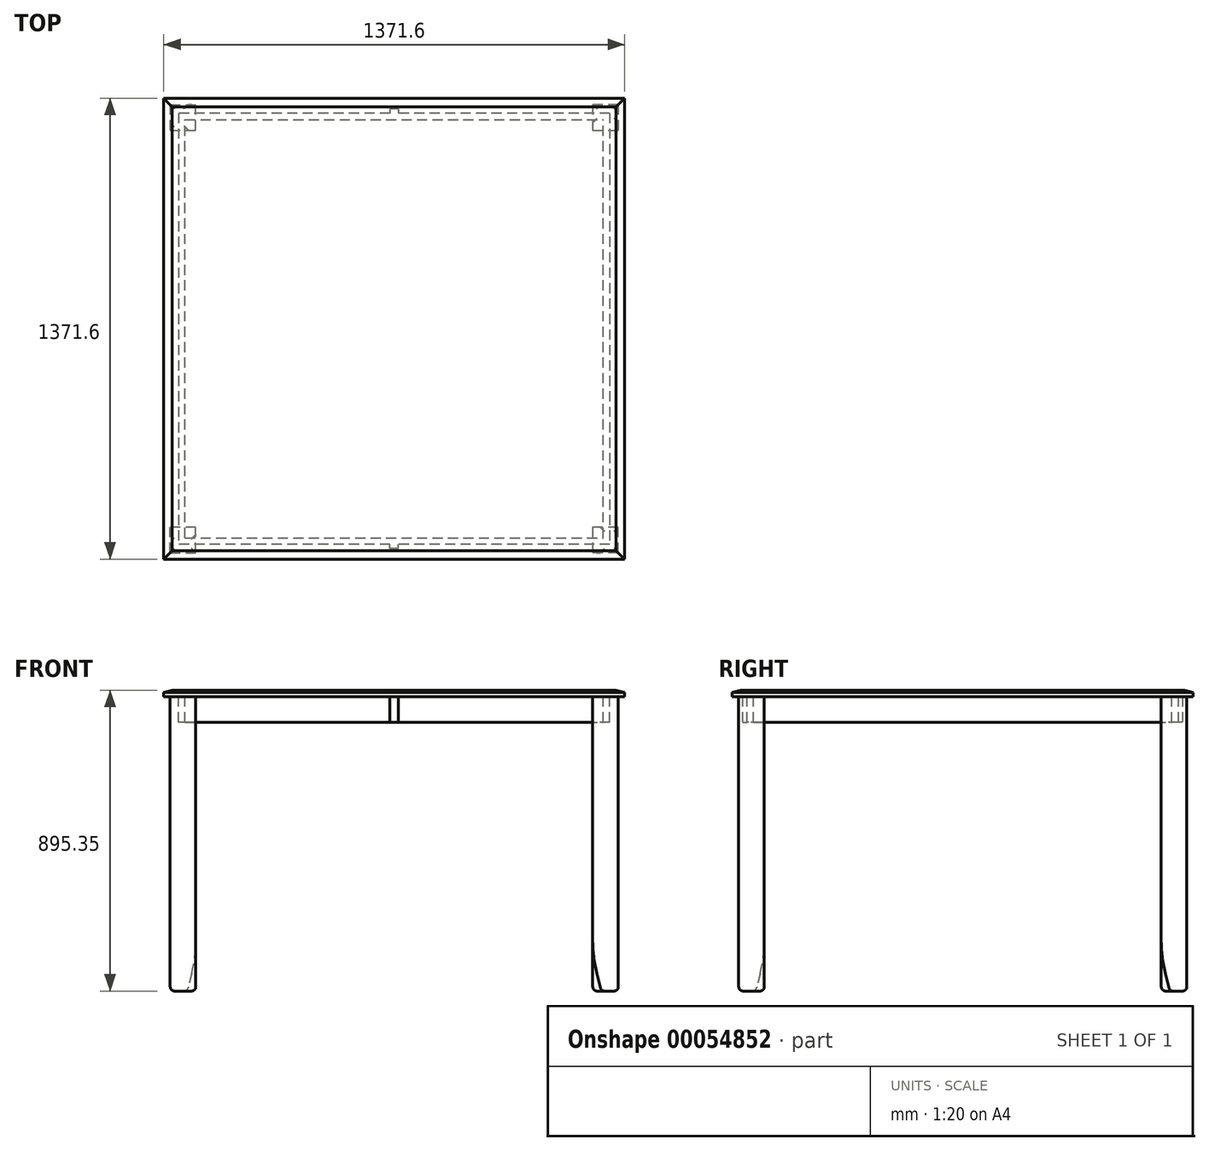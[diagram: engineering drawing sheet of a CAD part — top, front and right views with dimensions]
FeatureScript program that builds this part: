
annotation { "Feature Type Name" : "Feature", "Feature Type Description" : "" }
export const myFeature = defineFeature(function(context is Context, id is Id, definition is map)
    precondition{}
    {
        {
            var Q0;
            Q0=qCreatedBy(makeId("Top.planeOp"),FACE);
            var sketch = newSketch(context, id + "F0", { "sketchPlane" : qUnion([Q0])});
            skLineSegment(sketch, "E0.rect.bottom", {"start": v(685.8, 685.8) * mm, "end": v(-685.8, 685.8) * mm});
            skLineSegment(sketch, "E0.rect.top", {"start": v(685.8, -685.8) * mm, "end": v(-685.8, -685.8) * mm});
            skLineSegment(sketch, "E0.rect.left", {"start": v(685.8, 685.8) * mm, "end": v(685.8, -685.8) * mm});
            skLineSegment(sketch, "E0.rect.right", {"start": v(-685.8, 685.8) * mm, "end": v(-685.8, -685.8) * mm});
            skPoint(sketch, "E0.rect.middle", {"position": v(0, 0) * mm});
            skSolve(sketch);
        }
        {
            var Q0;
            Q0=qSketchRegion(id+"F0",true);
            extrude(context, id + "F1", {"entities" : qUnion([Q0]), "oppositeDirection" : true, "depth" : 19.05 * mm});
        }
        {
            var Q0;
            Q0=makeQuery(id+"F1.opExtrude","CAP_FACE",FACE,{"disambiguationData":[OSD([sQuery(id+"F0.wireOp",EDGE,"E0.rect.bottom"),sQuery(id+"F0.wireOp",EDGE,"E0.rect.top"),sQuery(id+"F0.wireOp",EDGE,"E0.rect.left"),sQuery(id+"F0.wireOp",EDGE,"E0.rect.right")])],"isStart":false});
            var sketch = newSketch(context, id + "F2", { "sketchPlane" : qUnion([Q0])});
            skLineSegment(sketch, "E1.rect.bottom", {"start": v(641.35, -641.35) * mm, "end": v(-641.35, -641.35) * mm});
            skLineSegment(sketch, "E1.rect.top", {"start": v(641.35, 641.35) * mm, "end": v(-641.35, 641.35) * mm});
            skLineSegment(sketch, "E1.rect.left", {"start": v(641.35, -641.35) * mm, "end": v(641.35, 641.35) * mm});
            skLineSegment(sketch, "E1.rect.right", {"start": v(-641.35, -641.35) * mm, "end": v(-641.35, 641.35) * mm});
            skPoint(sketch, "E1.rect.middle", {"position": v(0, 0) * mm});
            skLineSegment(sketch, "E2.rect.bottom", {"start": v(-622.3, 622.3) * mm, "end": v(622.3, 622.3) * mm});
            skLineSegment(sketch, "E2.rect.top", {"start": v(-622.3, -622.3) * mm, "end": v(622.3, -622.3) * mm});
            skLineSegment(sketch, "E2.rect.left", {"start": v(-622.3, 622.3) * mm, "end": v(-622.3, -622.3) * mm});
            skLineSegment(sketch, "E2.rect.right", {"start": v(622.3, 622.3) * mm, "end": v(622.3, -622.3) * mm});
            skSolve(sketch);
        }
        {
            var Q0;
            Q0=qSketchRegion(id+"F2",true);
            extrude(context, id + "F3", {"entities" : qUnion([Q0]), "operationType" : NewBodyOperationType.ADD, "depth" : 76.2 * mm});
        }
        {
            var Q0;
            {var subQ0=sQuery(id+"F0.wireOp",EDGE,"E0.rect.right");var subQ1=sQuery(id+"F0.wireOp",EDGE,"E0.rect.left");var subQ2=sQuery(id+"F0.wireOp",EDGE,"E0.rect.top");var subQ3=sQuery(id+"F0.wireOp",EDGE,"E0.rect.bottom");Q0=makeQuery(id+"F3.boolean.opBoolean","SPLIT",FACE,{"disambiguationData":[TD([makeQuery(id+"F1.opExtrude","SWEPT_FACE",FACE,{"disambiguationData":[OSD([subQ3])]})])],"derivedFrom":makeQuery(id+"F1.opExtrude","CAP_FACE",FACE,{"disambiguationData":[OSD([subQ3,subQ2,subQ1,subQ0])],"isStart":false})});}
            var sketch = newSketch(context, id + "F4", { "sketchPlane" : qUnion([Q0])});
            skLineSegment(sketch, "E3.bottom", {"start": v(-666.75, 666.75) * mm, "end": v(-590.55, 666.75) * mm});
            skLineSegment(sketch, "E3.top", {"start": v(-666.75, 590.55) * mm, "end": v(-590.55, 590.55) * mm});
            skLineSegment(sketch, "E3.left", {"start": v(-666.75, 666.75) * mm, "end": v(-666.75, 590.55) * mm});
            skLineSegment(sketch, "E3.right", {"start": v(-590.55, 666.75) * mm, "end": v(-590.55, 590.55) * mm});
            skSolve(sketch);
        }
        {
            var Q0;
            Q0=qSketchRegion(id+"F4",true);
            extrude(context, id + "F5", {"entities" : qUnion([Q0]), "depth" : 876.3 * mm});
        }
        {
            var Q0;
            Q0=qCreatedBy(makeId("Front.planeOp"),FACE);
            var sketch = newSketch(context, id + "F6", { "sketchPlane" : qUnion([Q0])});
            skLineSegment(sketch, "E4", {"start": v(0, 0) * mm, "end": v(0, -525.56) * mm, "construction": true});
            skSolve(sketch);
        }
        {
            var Q0;
            Q0=makeQuery(id+"F10.opPattern","COPY",EDGE,{"derivedFrom":makeQuery(id+"F5.opExtrude","CAP_EDGE",EDGE,{"disambiguationData":[OSD([sQuery(id+"F4.wireOp",EDGE,"E3.right")])],"isStart":false}),"instanceName":"2"});
            var Q1;
            Q1=makeQuery(id+"F5.opExtrude","CAP_EDGE",EDGE,{"disambiguationData":[OSD([sQuery(id+"F4.wireOp",EDGE,"E3.top")])],"isStart":false});
            chamfer(context, id + "F7", {"entities" : qUnion([Q0, Q1]), "chamferType" : ChamferType.TWO_OFFSETS, "width1" : 25.4 * mm, "oppositeDirection" : false, "width2" : 101.6 * mm, "tangentPropagation" : true});
        }
        {
            var Q0;
            Q0=makeQuery(id+"F5.opExtrude","CAP_FACE",FACE,{"disambiguationData":[OSD([sQuery(id+"F4.wireOp",EDGE,"E3.bottom"),sQuery(id+"F4.wireOp",EDGE,"E3.top"),sQuery(id+"F4.wireOp",EDGE,"E3.left"),sQuery(id+"F4.wireOp",EDGE,"E3.right")])],"isStart":false});
            fillet(context, id + "F8", {"entities" : qUnion([Q0]), "radius" : 12.7 * mm, "tangentPropagation" : true, "allowEdgeOverflow" : false});
        }
        {
            var Q0;
            {var subQ0=sQuery(id+"F4.wireOp",EDGE,"E3.top");Q0=makeQuery(id+"F7.opChamfer","BLEND_EDGE",EDGE,{"blendedFrom":[makeQuery(id+"F5.opExtrude","CAP_EDGE",EDGE,{"disambiguationData":[OSD([subQ0])],"isStart":false}),makeQuery(id+"F5.opExtrude","SWEPT_FACE",FACE,{"disambiguationData":[OSD([subQ0])]})],"blendedInto":[makeQuery(id+"F5.opExtrude","SWEPT_FACE",FACE,{"disambiguationData":[OSD([subQ0])]})]});}
            fillet(context, id + "F9", {"entities" : qUnion([Q0]), "radius" : 406.4 * mm, "tangentPropagation" : true, "allowEdgeOverflow" : false});
        }
        {
            var Q0;
            Q0=makeQuery(id+"F5.opExtrude","SWEPT_BODY",BODY,{"disambiguationData":[OSD([sQuery(id+"F4.wireOp",EDGE,"E3.bottom"),sQuery(id+"F4.wireOp",EDGE,"E3.top"),sQuery(id+"F4.wireOp",EDGE,"E3.left"),sQuery(id+"F4.wireOp",EDGE,"E3.right")])]});
            var Q1;
            Q1=sQuery(id+"F6.wireOp",EDGE,"E4");
            circularPattern(context, id + "F10", {"entities" : qUnion([Q0]), "axis" : qUnion([Q1]), "angle" : 360 * degree, "instanceCount" : round(4), "equalSpace" : true});
        }
        {
            var Q0;
            Q0=makeQuery(id+"F1.opExtrude","CAP_FACE",FACE,{"disambiguationData":[OSD([sQuery(id+"F0.wireOp",EDGE,"E0.rect.bottom"),sQuery(id+"F0.wireOp",EDGE,"E0.rect.top"),sQuery(id+"F0.wireOp",EDGE,"E0.rect.left"),sQuery(id+"F0.wireOp",EDGE,"E0.rect.right")])],"isStart":true});
            chamfer(context, id + "F11", {"entities" : qUnion([Q0]), "chamferType" : ChamferType.TWO_OFFSETS, "width1" : 6.35 * mm, "oppositeDirection" : true, "width2" : 25.4 * mm, "tangentPropagation" : true});
        }
        {
            var Q0;
            Q0=makeQuery(id+"F3.opExtrude","SWEPT_FACE",FACE,{"disambiguationData":[OSD([sQuery(id+"F2.wireOp",EDGE,"E1.rect.top")])]});
            var sketch = newSketch(context, id + "F12", { "sketchPlane" : qUnion([Q0])});
            skLineSegment(sketch, "E5.bottom", {"start": v(-12.7, -95.25) * mm, "end": v(12.7, -95.25) * mm});
            skLineSegment(sketch, "E5.top", {"start": v(-12.7, -19.05) * mm, "end": v(12.7, -19.05) * mm});
            skLineSegment(sketch, "E5.left", {"start": v(-12.7, -95.25) * mm, "end": v(-12.7, -19.05) * mm});
            skLineSegment(sketch, "E5.right", {"start": v(12.7, -95.25) * mm, "end": v(12.7, -19.05) * mm});
            skLineSegment(sketch, "E6", {"start": v(0, 0) * mm, "end": v(0, -95.25) * mm, "construction": true});
            skPoint(sketch, "E6.startSnap0", {"position": v(0, -19.05) * mm});
            skSolve(sketch);
        }
        {
            var Q0;
            Q0=makeQuery(id+"F12.imprint","IMPRINT",FACE,{"disambiguationData":[TD([[makeQuery(id+"F12.imprint","IMPRINT",EDGE,{"derivedFrom":sQuery(id+"F12.wireOp",EDGE,"E5.bottom")}),-1.0]])]});
            extrude(context, id + "F13", {"entities" : qUnion([Q0]), "operationType" : NewBodyOperationType.ADD, "depth" : 12.7 * mm});
        }
        {
            var Q0;
            Q0=makeQuery(id+"F3.opExtrude","SWEPT_FACE",FACE,{"disambiguationData":[OSD([sQuery(id+"F2.wireOp",EDGE,"E1.rect.bottom")])]});
            var sketch = newSketch(context, id + "F14", { "sketchPlane" : qUnion([Q0])});
            skLineSegment(sketch, "E7.bottom", {"start": v(-12.7, -19.05) * mm, "end": v(12.7, -19.05) * mm});
            skLineSegment(sketch, "E7.top", {"start": v(-12.7, -95.25) * mm, "end": v(12.7, -95.25) * mm});
            skLineSegment(sketch, "E7.left", {"start": v(-12.7, -19.05) * mm, "end": v(-12.7, -95.25) * mm});
            skLineSegment(sketch, "E7.right", {"start": v(12.7, -19.05) * mm, "end": v(12.7, -95.25) * mm});
            skSolve(sketch);
        }
        {
            var Q0;
            Q0=qSketchRegion(id+"F14",true);
            extrude(context, id + "F15", {"entities" : qUnion([Q0]), "operationType" : NewBodyOperationType.ADD, "depth" : 12.7 * mm});
        }
    });
